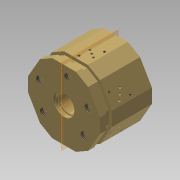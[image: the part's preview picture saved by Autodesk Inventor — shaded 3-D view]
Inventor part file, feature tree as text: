
AUTODESK INVENTOR PART (.ipt)
format: ipt  version: 2014 (Build 180170000, 170)  size: 517,120 bytes
history: native  units: mm
features: sketch x23, extrude x18, thread x10, pattern_circular x4, hole x3, other x2, chamfer x2, revolve x1
ambient origin geometry x8: Origin, YZ Plane, XZ Plane, XY Plane, X Axis, Y Axis, Z Axis, Center Point
bodies: body (feature_tree), Solid1 (feature_tree)
feature tree (63):
  other  "CrossSection1"
  other  "CrossSection2"
  extrude  "big opening"  Depth=35.0mm TaperAngle=0.0deg
  extrude  "chamber"  Depth=13.0mm TaperAngle=0.0deg
  extrude  "small opening"  Depth=5.0mm TaperAngle=0.0deg
  extrude  "bore to chamber - NC odor valve"  Depth=8.0mm TaperAngle=0.0deg
  extrude  "odor in - COM odor valve"  Depth=21.75mm TaperAngle=0.0deg
  extrude  "waste - NO odor valve"  Depth=6.0mm TaperAngle=0.0deg
  sketch  "Sketch14"  dims[d46=5.0mm]
  sketch  "Sketch24"  dims[d47=6.0mm]
  sketch  "Sketch27"  dims[d80=5.0mm]
  hole  "valve screws"  [1 undecoded]
  pattern_circular  "odor valves"  Count=3 Angle=120.0deg
  chamfer  "Chamfer1"  Distance=2.0mm Angle=45.0deg
  sketch  "Sketch32"  dims[d81=6.0mm]
  sketch  "Sketch33"  dims[d107=1.567mm d108=6.0mm d109=4.0mm d110=2.0mm d111=90.0deg d112=4.0mm d113=20.594885mm d139=30.0mm d140=120.0deg d143=5.5mm d144=2.0mm d145=45.0deg]
  extrude  "cable 1"  Depth=2.0mm TaperAngle=0.0deg
  extrude  "cable 2"  Depth=2.0mm TaperAngle=45.0deg
  pattern_circular  "cable path"  Count=3 Angle=120.0deg
  sketch  "Sketch38"  dims[d190=2.0mm d191=0.0mm d192=2.0mm d193=0.0mm]
  extrude  "Extrusion30"  Depth=3.18mm
  extrude  "Extrusion31"  Depth=3.18mm
  extrude  "Extrusion32"  Depth=4.0mm
  extrude  "Extrusion33"  Depth=4.0mm
  pattern_circular  "Circular Pattern9"  [2 undecoded]
  hole  "Hole6"  [1 undecoded]
  extrude  "Extrusion34"  Depth=1.0mm
  extrude  "Extrusion35"  Depth=13.07mm TaperAngle=0.0deg
  extrude  "Extrusion36"  Depth=2.0mm TaperAngle=0.0deg
  extrude  "Extrusion37"  Depth=1.0mm
  extrude  "Extrusion38"  Depth=17.84mm TaperAngle=0.0deg
  chamfer  "Chamfer2"  Angle=90.0deg  [1 undecoded]
  revolve  "Revolution2"  [1 undecoded]
  extrude  "Extrusion39"  Depth=1.0mm TaperAngle=0.0deg
  pattern_circular  "Circular Pattern12"  Count=2  [1 undecoded]
  thread  "Thread15"  [1 undecoded]
  thread  "Thread16"  [1 undecoded]
  thread  "Thread17"  [1 undecoded]
  thread  "Thread18"  [1 undecoded]
  thread  "Thread19"  [1 undecoded]
  thread  "Thread20"  [1 undecoded]
  thread  "Thread21"  [1 undecoded]
  thread  "Thread22"  [1 undecoded]
  thread  "Thread23"  [1 undecoded]
  thread  "Thread24"  [1 undecoded]
  hole  "Hole8"  [1 undecoded]
  sketch  "Sketch1"  dims[d0=27.0mm d2=35.0mm d3=0.0mm]
  sketch  "Sketch2"  dims[d4=13.0mm d5=15.0mm d6=0.0mm]
  sketch  "Sketch3"  dims[d7=4.0mm d8=5.0mm d9=0.0mm]
  sketch  "Sketch4"  dims[d10=8.0mm d11=15.0mm d12=0.0mm]
  sketch  "Sketch5"  dims[d13=1.5mm d14=21.75mm d15=0.0mm]
  sketch  "Sketch6"  dims[d16=1.5mm d18=6.0mm d19=0.0mm]
  sketch  "Sketch7"  dims[d20=1.5mm d22=6.0mm d23=0.0mm]
  sketch  "Sketch39"  dims[d195=60.0mm d196=360.0deg]
  sketch  "Sketch40"  dims[d209=0.5mm d210=2.0mm d211=0.0mm d212=20.0mm d213=0.5mm d214=2.0mm d215=0.0mm d216=20.0mm d242=0.5mm d243=2.0mm d244=45.0deg]
  sketch  "Sketch43"  dims[d246=2.0mm d247=0.0mm]
  sketch  "Sketch44"  dims[d250=1.5mm]
  sketch  "Sketch45"  dims[d251=14.66mm d252=0.0mm]
  sketch  "Sketch46"  dims[d253=2.0mm d254=0.0mm]
  sketch  "Sketch47"  dims[d257=1.5mm]
  sketch  "Sketch48"  dims[d258=19.43mm d259=0.0mm d260=30.0mm d261=120.0deg]
  sketch  "Sketch49"  dims[d287=3.18mm d290=6.325mm]
  sketch  "Sketch51"  dims[d291=6.325mm d292=3.18mm d296=4.0mm d299=4.0mm d303=1.567mm d304=6.0mm d305=4.0mm d306=2.0mm d307=90.0deg d308=4.0mm d309=20.594885mm d310=6.0mm d311=0.0mm d312=2.0mm d313=0.0mm d314=1.5mm d315=13.07mm d316=0.0mm d317=2.0mm d318=0.0mm d319=1.5mm d320=17.84mm d321=0.0mm d325=90.0deg d326=1.5mm d327=21.75mm d328=0.0mm d329=20.0mm d330=-10.471976mm d332=10.0mm d333=0.0mm d334=10.0mm d335=0.0mm d336=10.0mm d337=0.0mm d338=10.0mm d339=0.0mm d340=10.0mm d341=0.0mm d342=10.0mm d343=0.0mm d344=10.0mm d345=0.0mm d346=10.0mm d347=0.0mm d348=10.0mm d349=0.0mm d350=10.0mm d351=0.0mm d353=30.0deg d354=90.0deg d362=4.0mm d363=4.0mm d366=10.0mm d367=8.0mm d368=4.134mm d369=6.0mm d370=4.0mm d371=2.0mm d372=90.0deg d373=8.0mm d374=20.594885mm d88=1.0mm d89=1.0mm]
note: 18 required parameter values undecoded (feature->parameter linkage not recoverable at this tier; creation-order binding heuristic only, values carry confidence <= 0.55)